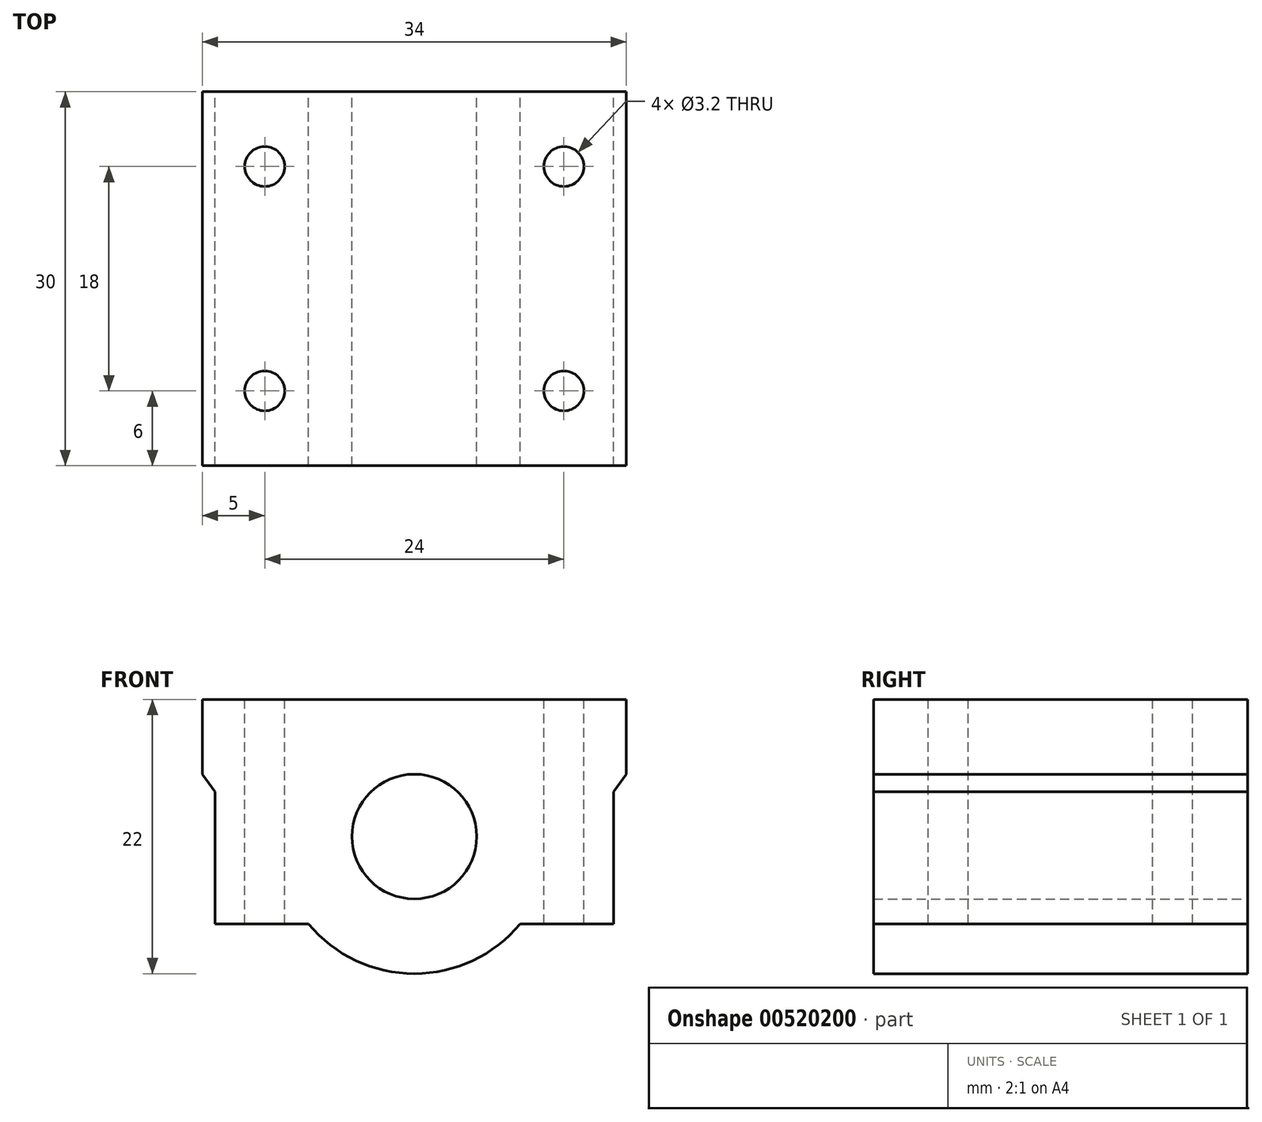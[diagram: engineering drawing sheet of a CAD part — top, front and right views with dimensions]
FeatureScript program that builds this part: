
annotation { "Feature Type Name" : "Feature", "Feature Type Description" : "" }
export const myFeature = defineFeature(function(context is Context, id is Id, definition is map)
    precondition{}
    {
        {
            var Q0;
            Q0=qCreatedBy(makeId("Front.planeOp"),FACE);
            var sketch = newSketch(context, id + "F0", { "sketchPlane" : qUnion([Q0])});
            skCircle(sketch, "E0", {"center": v(0, 0) * mm, "radius": 5 * mm});
            skArc(sketch, "E1", {"start": v(-8.49, -7) * mm, "mid": v(0, -11) * mm, "end": v(8.49, -7) * mm});
            skLineSegment(sketch, "E2", {"start": v(8.49, -7) * mm, "end": v(16, -7) * mm});
            skLineSegment(sketch, "E3", {"start": v(16, -7) * mm, "end": v(16, 3.58) * mm});
            skLineSegment(sketch, "E4", {"start": v(16, 3.58) * mm, "end": v(17, 5) * mm});
            skLineSegment(sketch, "E5", {"start": v(17, 5) * mm, "end": v(17, 11) * mm});
            skLineSegment(sketch, "E6", {"start": v(17, 11) * mm, "end": v(0, 11) * mm});
            skLineSegment(sketch, "E7", {"start": v(0, 11) * mm, "end": v(0, 0) * mm, "construction": true});
            skLineSegment(sketch, "E8.MirrorCS", {"start": v(-17, 11) * mm, "end": v(0, 11) * mm});
            skLineSegment(sketch, "E9.MirrorCS", {"start": v(-17, 5) * mm, "end": v(-17, 11) * mm});
            skLineSegment(sketch, "E10.MirrorCS", {"start": v(-16, 3.58) * mm, "end": v(-17, 5) * mm});
            skLineSegment(sketch, "E11.MirrorCS", {"start": v(-8.49, -7) * mm, "end": v(-16, -7) * mm});
            skLineSegment(sketch, "E12.MirrorCS", {"start": v(-16, -7) * mm, "end": v(-16, 3.58) * mm});
            skLineSegment(sketch, "E13", {"start": v(0, -11) * mm, "end": v(-10.02, -11) * mm, "construction": true});
            skSolve(sketch);
        }
        {
            var Q0;
            Q0 = qSketchRegion(id + "F0", true);
            extrude(context, id + "F1", {"entities" : qUnion([Q0]), "endBound" : BoundingType.SYMMETRIC, "depth" : 30 * mm, "offsetDistance" : 25 * mm});
        }
        {
            var Q0;
            Q0=makeQuery(id+"F1.opExtrude","SWEPT_FACE",FACE,{"disambiguationData":[OSD([sQuery(id+"F0.wireOp",EDGE,"E6"),sQuery(id+"F0.wireOp",EDGE,"E8.MirrorCS")])]});
            var sketch = newSketch(context, id + "F2", { "sketchPlane" : qUnion([Q0])});
            skLineSegment(sketch, "E14", {"start": v(0, -15) * mm, "end": v(0, 15) * mm, "construction": true});
            skLineSegment(sketch, "E15", {"start": v(-17, 0) * mm, "end": v(17, 0) * mm, "construction": true});
            skCircle(sketch, "E16", {"center": v(-12, -9) * mm, "radius": 1.6 * mm});
            skCircle(sketch, "E17.MirrorC", {"center": v(12, -9) * mm, "radius": 1.6 * mm});
            skCircle(sketch, "E18.MirrorC", {"center": v(12, 9) * mm, "radius": 1.6 * mm});
            skCircle(sketch, "E19.MirrorC", {"center": v(-12, 9) * mm, "radius": 1.6 * mm});
            skSolve(sketch);
        }
        {
            var Q0;
            Q0 = qSketchRegion(id + "F2", true);
            extrude(context, id + "F3", {"entities" : qUnion([Q0]), "operationType" : NewBodyOperationType.REMOVE, "oppositeDirection" : true, "depth" : 25 * mm, "offsetDistance" : 25 * mm});
        }
    });
